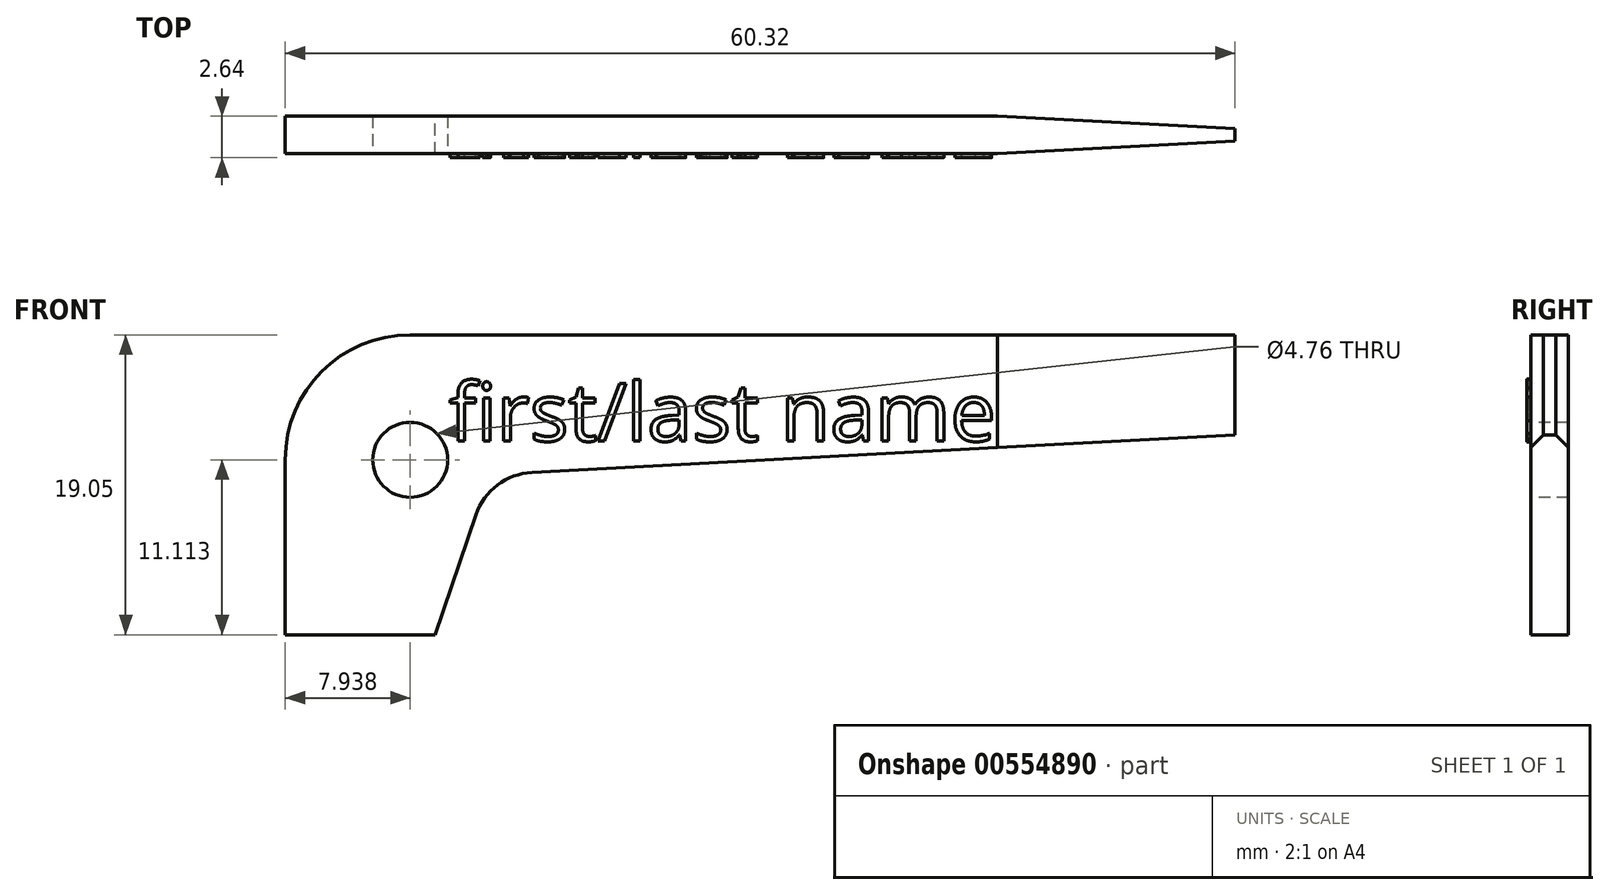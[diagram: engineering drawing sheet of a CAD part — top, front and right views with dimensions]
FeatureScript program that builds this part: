
annotation { "Feature Type Name" : "Feature", "Feature Type Description" : "" }
export const myFeature = defineFeature(function(context is Context, id is Id, definition is map)
    precondition{}
    {
        {
            var Q0;
            Q0=qCreatedBy(makeId("Front.planeOp"),FACE);
            var sketch = newSketch(context, id + "F0", { "sketchPlane" : qUnion([Q0])});
            skLineSegment(sketch, "E0.top", {"start": v(7.94, 19.05) * mm, "end": v(60.33, 19.05) * mm});
            skLineSegment(sketch, "E0.left", {"start": v(0, 0) * mm, "end": v(0, 11.11) * mm});
            skLineSegment(sketch, "E1", {"start": v(9.52, 0) * mm, "end": v(12.12, 7.63) * mm});
            skLineSegment(sketch, "E2", {"start": v(60.33, 12.7) * mm, "end": v(15.66, 10.31) * mm});
            skLineSegment(sketch, "E3", {"start": v(9.53, 0) * mm, "end": v(0, 0) * mm});
            skLineSegment(sketch, "E4", {"start": v(60.33, 12.7) * mm, "end": v(60.33, 19.05) * mm});
            skArc(sketch, "E5", {"start": v(15.66, 10.31) * mm, "mid": v(13.48, 9.51) * mm, "end": v(12.12, 7.63) * mm});
            skPoint(sketch, "E6.visualSharp", {"position": v(0, 19.05) * mm});
            skArc(sketch, "E6.filletArc", {"start": v(7.94, 19.05) * mm, "mid": v(2.32, 16.73) * mm, "end": v(0, 11.11) * mm});
            skSolve(sketch);
        }
        {
            var Q0;
            Q0 = qSketchRegion(id + "F0", true);
            extrude(context, id + "F1", {"entities" : qUnion([Q0]), "depth" : 2.38 * mm, "offsetDistance" : 25.4 * mm});
        }
        {
            var Q0;
            Q0=makeQuery(id+"F1.opExtrude","CAP_FACE",FACE,{"disambiguationData":[OSD([sQuery(id+"F0.wireOp",EDGE,"E0.top"),sQuery(id+"F0.wireOp",EDGE,"E0.left"),sQuery(id+"F0.wireOp",EDGE,"E1"),sQuery(id+"F0.wireOp",EDGE,"E2"),sQuery(id+"F0.wireOp",EDGE,"E3"),sQuery(id+"F0.wireOp",EDGE,"E4"),sQuery(id+"F0.wireOp",EDGE,"E5"),sQuery(id+"F0.wireOp",EDGE,"E6.filletArc")])],"isStart":false});
            var sketch = newSketch(context, id + "F2", { "sketchPlane" : qUnion([Q0])});
            skCircle(sketch, "E7", {"center": v(7.94, 11.11) * mm, "radius": 2.38 * mm});
            skSolve(sketch);
        }
        {
            var Q0;
            Q0=makeQuery(id+"F2.imprint","IMPRINT",FACE,{"disambiguationData":[TD([[makeQuery(id+"F2.imprint","IMPRINT",EDGE,{"derivedFrom":sQuery(id+"F2.wireOp",EDGE,"E7")}),1.0]])]});
            extrude(context, id + "F3", {"entities" : qUnion([Q0]), "operationType" : NewBodyOperationType.REMOVE, "oppositeDirection" : true, "depth" : 25.4 * mm, "offsetDistance" : 25.4 * mm});
        }
        {
            var Q0;
            Q0=makeQuery(id+"F1.opExtrude","SWEPT_FACE",FACE,{"disambiguationData":[OSD([sQuery(id+"F0.wireOp",EDGE,"E0.top")])]});
            var sketch = newSketch(context, id + "F4", { "sketchPlane" : qUnion([Q0])});
            skLineSegment(sketch, "E8", {"start": v(45.24, 0) * mm, "end": v(60.33, -0.8) * mm});
            skLineSegment(sketch, "E9", {"start": v(60.33, -0.8) * mm, "end": v(60.33, 0) * mm});
            skLineSegment(sketch, "E10", {"start": v(60.33, 0) * mm, "end": v(45.24, 0) * mm});
            skPoint(sketch, "E11.endSnap0", {"position": v(60.33, -1.2) * mm});
            skLineSegment(sketch, "E12.MirrorCS", {"start": v(45.24, -2.38) * mm, "end": v(60.33, -1.59) * mm});
            skLineSegment(sketch, "E13.MirrorCS", {"start": v(60.33, -2.38) * mm, "end": v(45.24, -2.38) * mm});
            skLineSegment(sketch, "E14.MirrorCS", {"start": v(60.33, -1.59) * mm, "end": v(60.33, -2.38) * mm});
            skSolve(sketch);
        }
        {
            var Q0;
            Q0=makeQuery(id+"F4.imprint","IMPRINT",FACE,{"disambiguationData":[TD([[makeQuery(id+"F4.imprint","IMPRINT",EDGE,{"derivedFrom":sQuery(id+"F4.wireOp",EDGE,"E12.MirrorCS")}),-1.0]])]});
            var Q1;
            Q1=makeQuery(id+"F4.imprint","IMPRINT",FACE,{"disambiguationData":[TD([[makeQuery(id+"F4.imprint","IMPRINT",EDGE,{"derivedFrom":sQuery(id+"F4.wireOp",EDGE,"E8")}),1.0]])]});
            extrude(context, id + "F5", {"entities" : qUnion([Q0, Q1]), "operationType" : NewBodyOperationType.REMOVE, "oppositeDirection" : true, "depth" : 25.4 * mm, "offsetDistance" : 25.4 * mm});
        }
        {
            var Q0;
            Q0=makeQuery(id+"F1.opExtrude","CAP_FACE",FACE,{"disambiguationData":[OSD([sQuery(id+"F0.wireOp",EDGE,"E0.top"),sQuery(id+"F0.wireOp",EDGE,"E0.left"),sQuery(id+"F0.wireOp",EDGE,"E1"),sQuery(id+"F0.wireOp",EDGE,"E2"),sQuery(id+"F0.wireOp",EDGE,"E3"),sQuery(id+"F0.wireOp",EDGE,"E4"),sQuery(id+"F0.wireOp",EDGE,"E5"),sQuery(id+"F0.wireOp",EDGE,"E6.filletArc")])],"isStart":false});
            var sketch = newSketch(context, id + "F6", { "sketchPlane" : qUnion([Q0])});
            skText(sketch, "E15", { "text": "first/last name", "fontName": "OpenSans-Regular.ttf"});
            const initialGuessF6  = {"E15": [0.0104, 0.0123, 1, 0, 0.0037]};
            skSetInitialGuess(sketch, initialGuessF6);
            skSolve(sketch);
        }
        {
            var Q0;
            Q0 = qSketchRegion(id + "F6", true);
            extrude(context, id + "F7", {"entities" : qUnion([Q0]), "operationType" : NewBodyOperationType.ADD, "depth" : 0.25 * mm, "offsetDistance" : 25.4 * mm});
        }
    });
